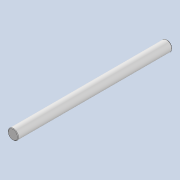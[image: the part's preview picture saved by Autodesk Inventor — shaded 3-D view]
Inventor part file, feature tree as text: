
AUTODESK INVENTOR PART (.ipt)
format: ipt  version: 2020 (Build 240168000, 168)  size: 91,136 bytes
history: native  units: mm
features: extrude x1, chamfer x1, sketch x1
ambient origin geometry x8: Origin, YZ Plane, XZ Plane, XY Plane, X Axis, Y Axis, Z Axis, Center Point
bodies: Solid1 (feature_tree)
feature tree (3):
  extrude  "Extrusion1"  Depth=150.0mm TaperAngle=0.0deg
  chamfer  "Chamfer1"  Distance=0.5mm Angle=45.0deg
  sketch  "Sketch1"  dims[d0=10.0mm d1=150.0mm d2=0.0mm d3=0.5mm d4=2.0mm d5=45.0deg]
